# Revit family: 2ICON2_MC_RFA
name_source: partatom
category: Data Devices
units: mm (PartAtom-declared; Revit-internal decimal feet)

## family parameters
Cut with Voids When Loaded = No
Host = Face
Maintain Annotation Orientation = No
OmniClass Number = 23.85.50.00
OmniClass Title = Communication Systems
Part Type = Normal
Room Calculation Point = No
Round Connector Dimension = Use Diameter
Shared = No

## types (7) — shared parameters
Body Material = Danfoss Plastic Dark Gray
Default Elevation = 1219 mm
Description = Main Controller and Room Thermostat
H = 120 mm  [stored 0.393701 ft]
IP Rating = IP 20
IfcExportAs = IfcElectricApplianceType
IfcExportType = ICON2_MC
L = 333 mm  [stored 1.09252 ft]
LOD 200 = No
LOD 350 = Yes
Manufacturer = Danfoss
Max Number of Thermostats = 15
Max Power Consumption Per Actuator = 2 W
Number of Actuator Output = 15
Output Voltage to Thermostats = 24 V DC
Power = 50 VA
Power Consumption = 50 W
Power Supply = 220-240 V AC
R1 = 2 mm  [stored 0.00656168 ft]
Transmission Frequency = 2,4 GHz (Zigbee 3.0)
Transmission Range = Up to 30 m
URL = https://store.danfoss.com
Voltage = 230 V
W = 52 mm

## per-type parameters (varying)
| type | Model | Model Type | Output Voltage to Actuators |
| Icon2_Main Controller_Basic_EU_088U2100 | 088U2100 | Icon2_Main Controller_Basic_EU | 230V (24V with conversion module installed) |
| Icon2_Main Controller_Basic_CH_088U2101 | 088U2101 | Icon2_Main Controller_Basic_CH | 230V (24V with conversion module installed) |
| Icon2_Main Controller_Basic_NP_088U2102 | 088U2102 | Icon2_Main Controller_Basic_NP | 230V (24V with conversion module installed) |
| Icon2_Main Controller_Advanced_EU_088U2110 | 088U2110 | Icon2_Main Controller_Advanced_EU | 230V (24V with conversion module installed) |
| Icon2_Main Controller_Advanced_CH_088U2111 | 088U2111 | Icon2_Main Controller_Advanced_CH | 230V (24V with conversion module installed) |
| Icon2_Main Controller_Advanced_NP_088U2112 | 088U2112 | Icon2_Main Controller_Advanced_NP | 230V (24V with conversion module installed) |
| Icon2_Main Controller_Basic_24V_EU_088U2105 | 088U2105 | Icon2_Main Controller_Basic_24V_EU | 24V with conversion module installed |

note: [stored X ft] marks values corroborated as IEEE doubles in the binary element streams (Revit-internal decimal feet)

## geometry (parser evidence)
native form markers: Sweep x3
no freeform markers — native parametric forms only
